FCSTD DOCUMENT  (FreeCAD 0.19R)
Label: pantin
License: All rights reserved
LicenseURL: http://en.wikipedia.org/wiki/All_rights_reserved
objects: Part::FeaturePython×25, Part::Vertex×23, App::Placement×4, App::DocumentObjectGroup×3, App::FeaturePython×1
note: 48 computed .brp shape members not serialized (recipe doc carries the construction recipe); baked Part::Feature solids carry a one-line shape summary decoded from their .brp

FEATURE [Part::Vertex] Vertex033  label="Vertex Rotule droite"
  AttacherType = Attacher::AttachEngine3D
  Placement = pos=(11,9,79) rot=(-1,0,0;0.306691rad)
  X = 0
  Y = 0
  Z = 0
FEATURE [Part::Vertex] Vertex016  label="Vertex Poigné gauche"
  AttacherType = Attacher::AttachEngine3D
  Placement = pos=(-30,0,148) rot=(0,0,1;0rad)
  X = 0
  Y = 0
  Z = 0
FEATURE [Part::Vertex] Vertex006  label="Vertex Epaule droite"
  AttacherType = Attacher::AttachEngine3D
  Placement = pos=(29,0,234) rot=(0,0,1;0rad)
  X = 0
  Y = 0
  Z = 0
FEATURE [Part::Vertex] Vertex014  label="Vertex Poigné droit"
  AttacherType = Attacher::AttachEngine3D
  Placement = pos=(30,0,148) rot=(0,0,1;0rad)
  X = 0
  Y = 0
  Z = 0
FEATURE [Part::Vertex] Vertex044  label="Vertex Orteilles gauche"
  AttacherType = Attacher::AttachEngine3D
  Placement = pos=(-15,43,0) rot=(-0.940276,-0.336401,0.052111;0.326559rad)
  X = 0
  Y = 0
  Z = 0
FEATURE [Part::Vertex] Vertex029  label="Vertex Tete de femur droit"
  AttacherType = Attacher::AttachEngine3D
  Placement = pos=(11,9,138) rot=(-1,0,0;0.306691rad)
  X = 0
  Y = 0
  Z = 0
FEATURE [Part::Vertex] Vertex025  label="Vertex Bassin"
  AttacherType = Attacher::AttachEngine3D
  Placement = pos=(0,0,144) rot=(0,0,1;0rad)
  X = 0
  Y = 0
  Z = 0
FEATURE [Part::Vertex] Vertex011  label="Vertex Coude gauche"
  AttacherType = Attacher::AttachEngine3D
  Placement = pos=(-30,0,191) rot=(0,0,1;0rad)
  X = 0
  Y = 0
  Z = 0
FEATURE [Part::Vertex] Vertex018  label="Vertex Cou bas"
  AttacherType = Attacher::AttachEngine3D
  Placement = pos=(0,0,234) rot=(0,0,1;0rad)
  X = 0
  Y = 0
  Z = 0
FEATURE [Part::FeaturePython] Line023  label="Avant Bras Gauche"  # WARN: FeaturePython — macro-defined, semantics opaque (R4)
  Vertex1 = -> Vertex011 [Vertex1]
  Vertex2 = -> Vertex016 [Vertex1]
FEATURE [Part::FeaturePython] Line028  label="Bassin Droit"  # WARN: FeaturePython — macro-defined, semantics opaque (R4)
  Vertex1 = -> Vertex025 [Vertex1]
  Vertex2 = -> Vertex029 [Vertex1]
FEATURE [Part::FeaturePython] Line030  label="Femur Droit"  # WARN: FeaturePython — macro-defined, semantics opaque (R4)
  Vertex1 = -> Vertex029 [Vertex1]
  Vertex2 = -> Vertex033 [Vertex1]
FEATURE [Part::Vertex] Vertex031  label="Vertex Tete de femur gauche"
  AttacherType = Attacher::AttachEngine3D
  Placement = pos=(-11,9,138) rot=(-0.940276,-0.336401,0.052111;0.326559rad)
  X = 0
  Y = 0
  Z = 0
FEATURE [Part::FeaturePython] Line029  label="Bassin Gauche"  # WARN: FeaturePython — macro-defined, semantics opaque (R4)
  Vertex1 = -> Vertex025 [Vertex1]
  Vertex2 = -> Vertex031 [Vertex1]
FEATURE [Part::Vertex] Vertex012  label="Vertex Coude droit"
  AttacherType = Attacher::AttachEngine3D
  Placement = pos=(30,0,191) rot=(0,0,1;0rad)
  X = 0
  Y = 0
  Z = 0
FEATURE [Part::FeaturePython] Line020  label="Bras Droit"  # WARN: FeaturePython — macro-defined, semantics opaque (R4)
  Vertex1 = -> Vertex006 [Vertex1]
  Vertex2 = -> Vertex012 [Vertex1]
FEATURE [Part::FeaturePython] Line022  label="Avant Bras Droit"  # WARN: FeaturePython — macro-defined, semantics opaque (R4)
  Vertex1 = -> Vertex012 [Vertex1]
  Vertex2 = -> Vertex014 [Vertex1]
FEATURE [Part::Vertex] Vertex038  label="Vertex Cheville gauche"
  AttacherType = Attacher::AttachEngine3D
  Placement = pos=(-11,10,13) rot=(-0.940276,-0.336401,0.052111;0.326559rad)
  X = 0
  Y = 0
  Z = 0
FEATURE [Part::FeaturePython] Line037  label="Os Pied 2 gauche"  # WARN: FeaturePython — macro-defined, semantics opaque (R4)
  Vertex1 = -> Vertex038 [Vertex1]
  Vertex2 = -> Vertex044 [Vertex1]
FEATURE [Part::Vertex] Vertex043  label="Vertex Orteilles droits"
  AttacherType = Attacher::AttachEngine3D
  Placement = pos=(15,43,0) rot=(-1,0,0;0.306691rad)
  X = 0
  Y = 0
  Z = 0
FEATURE [Part::Vertex] Vertex023  label="Vertex Lombaires"
  AttacherType = Attacher::AttachEngine3D
  Placement = pos=(0,0,184) rot=(0,0,1;0rad)
  X = 0
  Y = 0
  Z = 0
FEATURE [Part::FeaturePython] Line026  label="Dos"  # WARN: FeaturePython — macro-defined, semantics opaque (R4)
  Vertex1 = -> Vertex018 [Vertex1]
  Vertex2 = -> Vertex023 [Vertex1]
FEATURE [Part::FeaturePython] Line040  label="Vertebres"  # WARN: FeaturePython — macro-defined, semantics opaque (R4)
  Vertex1 = -> Vertex023 [Vertex1]
  Vertex2 = -> Vertex025 [Vertex1]
FEATURE [Part::FeaturePython] Line041  label="Dos 2"  # WARN: FeaturePython — macro-defined, semantics opaque (R4)
  Vertex1 = -> Vertex006 [Vertex1]
  Vertex2 = -> Vertex023 [Vertex1]
FEATURE [Part::Vertex] Vertex042  label="Vertex Talon gauche"
  AttacherType = Attacher::AttachEngine3D
  Placement = pos=(-11,10,0) rot=(-0.940276,-0.336401,0.052111;0.326559rad)
  X = 0
  Y = 0
  Z = 0
FEATURE [Part::FeaturePython] Line017  label="Os Pied 1 gauche"  # WARN: FeaturePython — macro-defined, semantics opaque (R4)
  Vertex1 = -> Vertex042 [Vertex1]
  Vertex2 = -> Vertex044 [Vertex1]
FEATURE [Part::FeaturePython] Line036  label="Talon Gauche"  # WARN: FeaturePython — macro-defined, semantics opaque (R4)
  Vertex1 = -> Vertex038 [Vertex1]
  Vertex2 = -> Vertex042 [Vertex1]
FEATURE [Part::Vertex] Vertex037  label="Vertex Cheville droite"
  AttacherType = Attacher::AttachEngine3D
  Placement = pos=(11,10,13) rot=(-1,0,0;0.306691rad)
  X = 0
  Y = 0
  Z = 0
FEATURE [Part::FeaturePython] Line032  label="Tibia Droit"  # WARN: FeaturePython — macro-defined, semantics opaque (R4)
  Vertex1 = -> Vertex033 [Vertex1]
  Vertex2 = -> Vertex037 [Vertex1]
FEATURE [Part::FeaturePython] Line035  label="Os Pied 2 droit"  # WARN: FeaturePython — macro-defined, semantics opaque (R4)
  Vertex1 = -> Vertex037 [Vertex1]
  Vertex2 = -> Vertex043 [Vertex1]
FEATURE [Part::Vertex] Vertex041  label="Vertex Talon droit"
  AttacherType = Attacher::AttachEngine3D
  Placement = pos=(11,10,0) rot=(-1,0,0;0.306691rad)
  X = 0
  Y = 0
  Z = 0
FEATURE [Part::FeaturePython] Line016  label="Os Pied 1 droit"  # WARN: FeaturePython — macro-defined, semantics opaque (R4)
  Vertex1 = -> Vertex041 [Vertex1]
  Vertex2 = -> Vertex043 [Vertex1]
FEATURE [Part::FeaturePython] Line034  label="Talon Droit"  # WARN: FeaturePython — macro-defined, semantics opaque (R4)
  Vertex1 = -> Vertex037 [Vertex1]
  Vertex2 = -> Vertex041 [Vertex1]
FEATURE [Part::Vertex] Vertex022  label="Vertex Main gauche"
  AttacherType = Attacher::AttachEngine3D
  Placement = pos=(-30,0,127) rot=(0,0,1;0rad)
  X = 0
  Y = 0
  Z = 0
FEATURE [Part::FeaturePython] Line025  label="Main Gauche"  # WARN: FeaturePython — macro-defined, semantics opaque (R4)
  Vertex1 = -> Vertex016 [Vertex1]
  Vertex2 = -> Vertex022 [Vertex1]
FEATURE [Part::Vertex] Vertex  label="Vertex Tete"
  AttacherType = Attacher::AttachEngine3D
  Placement = pos=(0,0,285) rot=(0,0,1;0rad)
  X = 0
  Y = 0
  Z = 0
FEATURE [Part::Vertex] Vertex005  label="Vertex Epaule gauche"
  AttacherType = Attacher::AttachEngine3D
  Placement = pos=(-29,0,234) rot=(0,0,1;0rad)
  X = 0
  Y = 0
  Z = 0
FEATURE [Part::FeaturePython] Line018  label="Epaules"  # WARN: FeaturePython — macro-defined, semantics opaque (R4)
  Vertex1 = -> Vertex006 [Vertex1]
  Vertex2 = -> Vertex005 [Vertex1]
FEATURE [Part::FeaturePython] Line021  label="Bras Gauche"  # WARN: FeaturePython — macro-defined, semantics opaque (R4)
  Vertex1 = -> Vertex005 [Vertex1]
  Vertex2 = -> Vertex011 [Vertex1]
FEATURE [Part::FeaturePython] Line042  label="Dos 3"  # WARN: FeaturePython — macro-defined, semantics opaque (R4)
  Vertex1 = -> Vertex005 [Vertex1]
  Vertex2 = -> Vertex023 [Vertex1]
FEATURE [Part::Vertex] Vertex021  label="Vertex Main droite"
  AttacherType = Attacher::AttachEngine3D
  Placement = pos=(30,0,128) rot=(0,0,1;0rad)
  X = 0
  Y = 0
  Z = 0
FEATURE [Part::FeaturePython] Line024  label="Main Droite"  # WARN: FeaturePython — macro-defined, semantics opaque (R4)
  Vertex1 = -> Vertex014 [Vertex1]
  Vertex2 = -> Vertex021 [Vertex1]
FEATURE [Part::Vertex] Vertex002  label="Vertex Cou cervicales"
  AttacherType = Attacher::AttachEngine3D
  Placement = pos=(0,0,247) rot=(0,0,1;0rad)
  X = 0
  Y = 0
  Z = 0
FEATURE [Part::FeaturePython] Line  label="Crane"  # WARN: FeaturePython — macro-defined, semantics opaque (R4)
  Vertex1 = -> Vertex002 [Vertex1]
  Vertex2 = -> Vertex [Vertex1]
FEATURE [Part::FeaturePython] Line019  label="Cervicales"  # WARN: FeaturePython — macro-defined, semantics opaque (R4)
  Vertex1 = -> Vertex018 [Vertex1]
  Vertex2 = -> Vertex002 [Vertex1]
FEATURE [Part::Vertex] Vertex034  label="Vertex Rotule gauche"
  AttacherType = Attacher::AttachEngine3D
  Placement = pos=(-11,9,79) rot=(-0.940276,-0.336401,0.052111;0.326559rad)
  X = 0
  Y = 0
  Z = 0
FEATURE [App::DocumentObjectGroup] Group001  label="Points"
  Group = -> [Vertex,Vertex002,Vertex005,Vertex006,Vertex011,Vertex012,Vertex014,Vertex016,Vertex018,Vertex021,Vertex022,Vertex023,Vertex025,Vertex029,Vertex031,Vertex033,Vertex034,Vertex037,Vertex038,Vertex041,Vertex042,Vertex043,Vertex044]
FEATURE [Part::FeaturePython] Line031  label="Femur Gauche"  # WARN: FeaturePython — macro-defined, semantics opaque (R4)
  Vertex1 = -> Vertex031 [Vertex1]
  Vertex2 = -> Vertex034 [Vertex1]
FEATURE [Part::FeaturePython] Line033  label="Tibia Gauche"  # WARN: FeaturePython — macro-defined, semantics opaque (R4)
  Vertex1 = -> Vertex034 [Vertex1]
  Vertex2 = -> Vertex038 [Vertex1]
FEATURE [App::DocumentObjectGroup] WorkAxis_P  label="Os"
  Group = -> [Line,Line018,Line019,Line020,Line021,Line022,Line023,Line024,Line025,Line026,Line028,Line029,Line030,Line031,Line032,Line033,Line034,Line016,Line017,Line035,Line037,Line036,Line040,Line041,Line042]
FEATURE [App::FeaturePython] PDInclude  label="IKComputation"  # WARN: FeaturePython — macro-defined, semantics opaque (R4)
FEATURE [App::Placement] CibleMD
  Placement = pos=(30,0,128) rot=(-0.940276,-0.336401,0.052111;0rad)
FEATURE [App::Placement] CibleMD001  label="CibleMG"
  Placement = pos=(-30,0,127) rot=(0,0,1;0rad)
FEATURE [App::Placement] CibleMD002  label="CibleOD"
  Placement = pos=(15,43,0) rot=(0,0,1;0rad)
FEATURE [App::Placement] CibleMD003  label="CibleOG"
  Placement = pos=(-15,43,0) rot=(0,0,1;0rad)
FEATURE [App::DocumentObjectGroup] Group  label="Cibles"
  Group = -> [CibleMD,CibleMD001,CibleMD002,CibleMD003]
